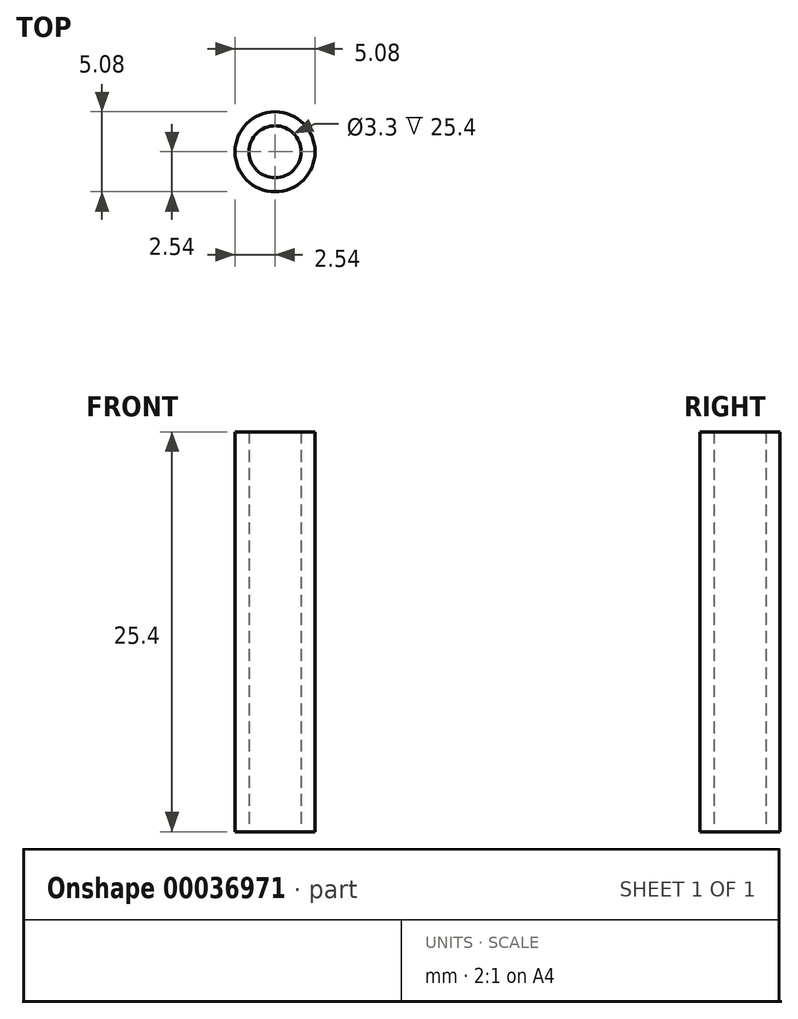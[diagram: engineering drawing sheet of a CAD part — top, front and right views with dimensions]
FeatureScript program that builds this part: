
annotation { "Feature Type Name" : "Feature", "Feature Type Description" : "" }
export const myFeature = defineFeature(function(context is Context, id is Id, definition is map)
    precondition{}
    {
        {
            var Q0;
            Q0=qCreatedBy(makeId("Top.planeOp"),FACE);
            var sketch = newSketch(context, id + "F0", { "sketchPlane" : qUnion([Q0])});
            skCircle(sketch, "E0", {"center": v(0, 0) * mm, "radius": 1.65 * mm});
            skCircle(sketch, "E1.0", {"center": v(0, 0) * mm, "radius": 2.54 * mm});
            skSolve(sketch);
        }
        {
            var Q0;
            Q0 = qSketchRegion(id + "F0", true);
            extrude(context, id + "F1", {"entities" : qUnion([Q0]), "depth" : 25.4 * mm});
        }
    });
